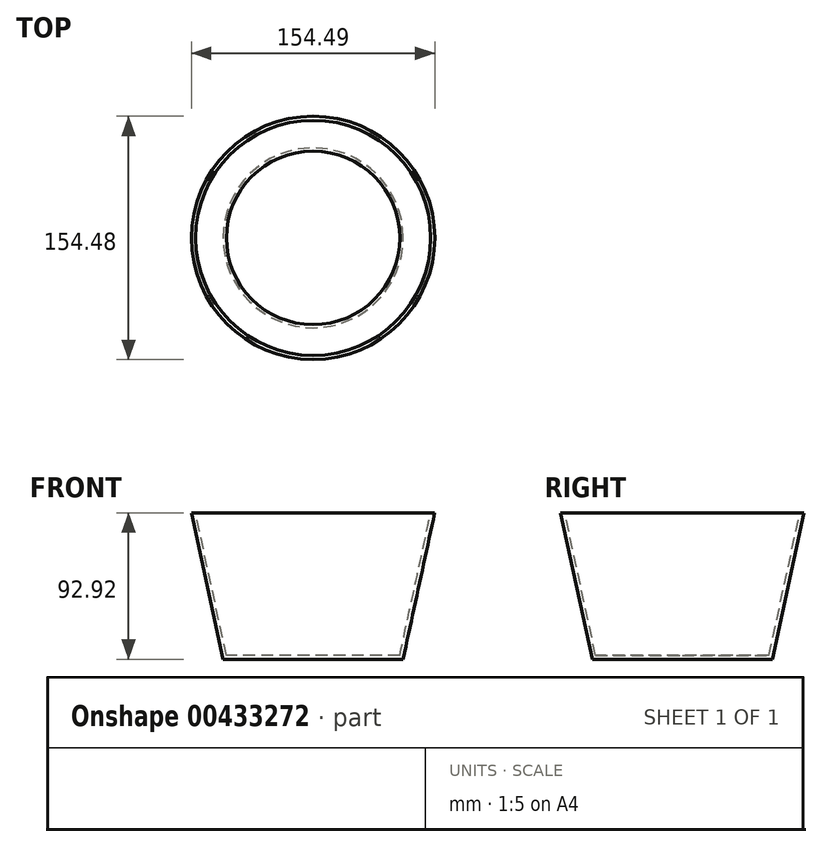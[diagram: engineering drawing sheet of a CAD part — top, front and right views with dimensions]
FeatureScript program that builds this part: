
annotation { "Feature Type Name" : "Feature", "Feature Type Description" : "" }
export const myFeature = defineFeature(function(context is Context, id is Id, definition is map)
    precondition{}
    {
        {
            var Q0;
            Q0=qCreatedBy(makeId("Front.planeOp"),FACE);
            var sketch = newSketch(context, id + "F0", { "sketchPlane" : qUnion([Q0])});
            skLineSegment(sketch, "E0", {"start": v(-41.85, 48.67) * mm, "end": v(35.4, 48.67) * mm});
            skLineSegment(sketch, "E1", {"start": v(-41.85, 48.67) * mm, "end": v(-41.85, -44.25) * mm});
            skLineSegment(sketch, "E2", {"start": v(-41.85, -44.25) * mm, "end": v(15.3, -44.25) * mm});
            skLineSegment(sketch, "E3", {"start": v(35.4, 48.67) * mm, "end": v(15.3, -44.25) * mm});
            skSolve(sketch);
        }
        {
            var Q0;
            Q0 = qSketchRegion(id + "F0", true);
            var Q1;
            Q1=sQuery(id+"F0.wireOp",EDGE,"E1");
            revolve(context, id + "F1", {"entities" : qUnion([Q0]), "axis" : qUnion([Q1]), "revolveType" : RevolveType.FULL});
        }
        {
            var Q0;
            Q0=makeQuery(id+"F1.opRevolve","SWEPT_FACE",FACE,{"disambiguationData":[OSD([sQuery(id+"F0.wireOp",EDGE,"E0")])]});
            shell(context, id + "F2", {"entities" : qUnion([Q0]), "thickness" : 2.54 * mm});
        }
    });
